# Revit family: HERO-3000-xxx-SFx
name_source: partatom
category: Oprawy oświetleniowe
revit_build: Autodesk Revit 2017 (Build: 20190507_1515(x64)
units: mm (PartAtom-declared; Revit-internal decimal feet)

## family parameters
Numer OmniClass = 23.80.70.11
Obiekt nadrzędny = Powierzchnia
Punkt obliczania pomieszczeń = Nie
Tnij formami wycięć po wczytaniu = Nie
Typ części = Normalny
Tytuł OmniClass = Luminaries for Internal Lighting
Współdzielony = Nie
Wymiar okrągłego złącza = Użyj średnicy
Źródło światła = Tak

## types (4) — shared parameters
Emituj kształt widoczny w renderingu = Nie
Emituj z długości prostokąta = 360 mm  [stored 1.1811 ft]
Emituj z szerokości prostokąta = 587 mm  [stored 1.92585 ft]
Filtr koloru = 16777215
Kod zespołu = D5020200
Lampa = LED
Obciążenie pozorne = 244 VA
Odchylenie kierunku = 90.00°
Plik sieci fotometrycznej = HERO 1500-840 SF-DA.IES
Producent = RIDI Leuchten GmbH
URL = www.ridi.de
Zmiana temperatury barwowej przyciemniania lampy = <Brak>
brand = RIDI
conformity mark = CE
electrical safety class = 1
height = 110 mm  [stored 0.360892 ft]
ingress protection (IP) code = IP64
length = 627 mm  [stored 2.05709 ft]
nominal frequency = 50-60Hz
nominal voltage = 230
rated input power = 244
voltage type (AC, DC, UC) = AC
weight = 14 kg
width = 372 mm  [stored 1.22047 ft]
zero-valued in all types: Domyślna rzędna

## per-type parameters (varying)
| type | Model |
| HERO 3000-840 SF | 0657459 |
| HERO 3000-840 SF-DA | 0667459 |
| HERO 3000-865 SF | 0657460 |
| HERO 3000-865 SF-DA | 0667460 |

note: column(s) folded — value = type name in every type: product name

note: [stored X ft] marks values corroborated as IEEE doubles in the binary element streams (Revit-internal decimal feet)
